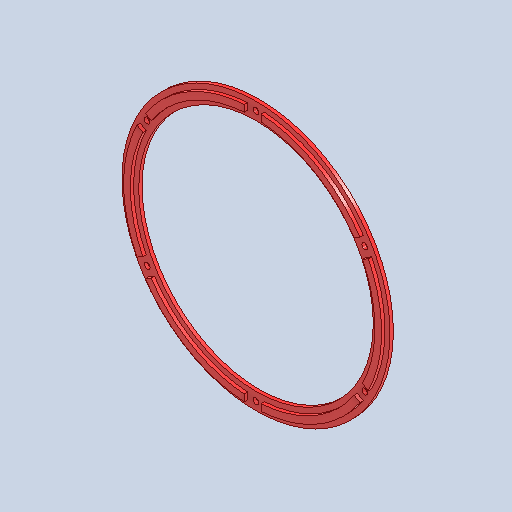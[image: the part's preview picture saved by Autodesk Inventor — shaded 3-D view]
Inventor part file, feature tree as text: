
AUTODESK INVENTOR PART (.ipt)
format: ipt  version: 2024 (Build 280153000, 153)  size: 207,872 bytes
history: native  units: mm
features: sketch x4, extrude x3, pattern_circular x2, other x1, hole x1
ambient origin geometry x8: Origin, YZ Plane, XZ Plane, XY Plane, X Axis, Y Axis, Z Axis, Center Point
bodies: Body1 (feature_tree)
feature tree (11):
  other  "ソリッド1"
  extrude  "押し出し1"  Depth=160.0mm
  hole  "穴1"  [1 undecoded]
  pattern_circular  "円形状パターン1"  [2 undecoded]
  extrude  "押し出し2"  Depth=75.0mm
  extrude  "押し出し3"  Depth=60.0mm TaperAngle=360.0deg
  pattern_circular  "円形状パターン2"  [2 undecoded]
  sketch  "スケッチ1"
  sketch  "スケッチ2"
  sketch  "スケッチ3"
  sketch  "スケッチ4"
note: 5 required parameter values undecoded (feature->parameter linkage not recoverable at this tier; creation-order binding heuristic only, values carry confidence <= 0.55)
